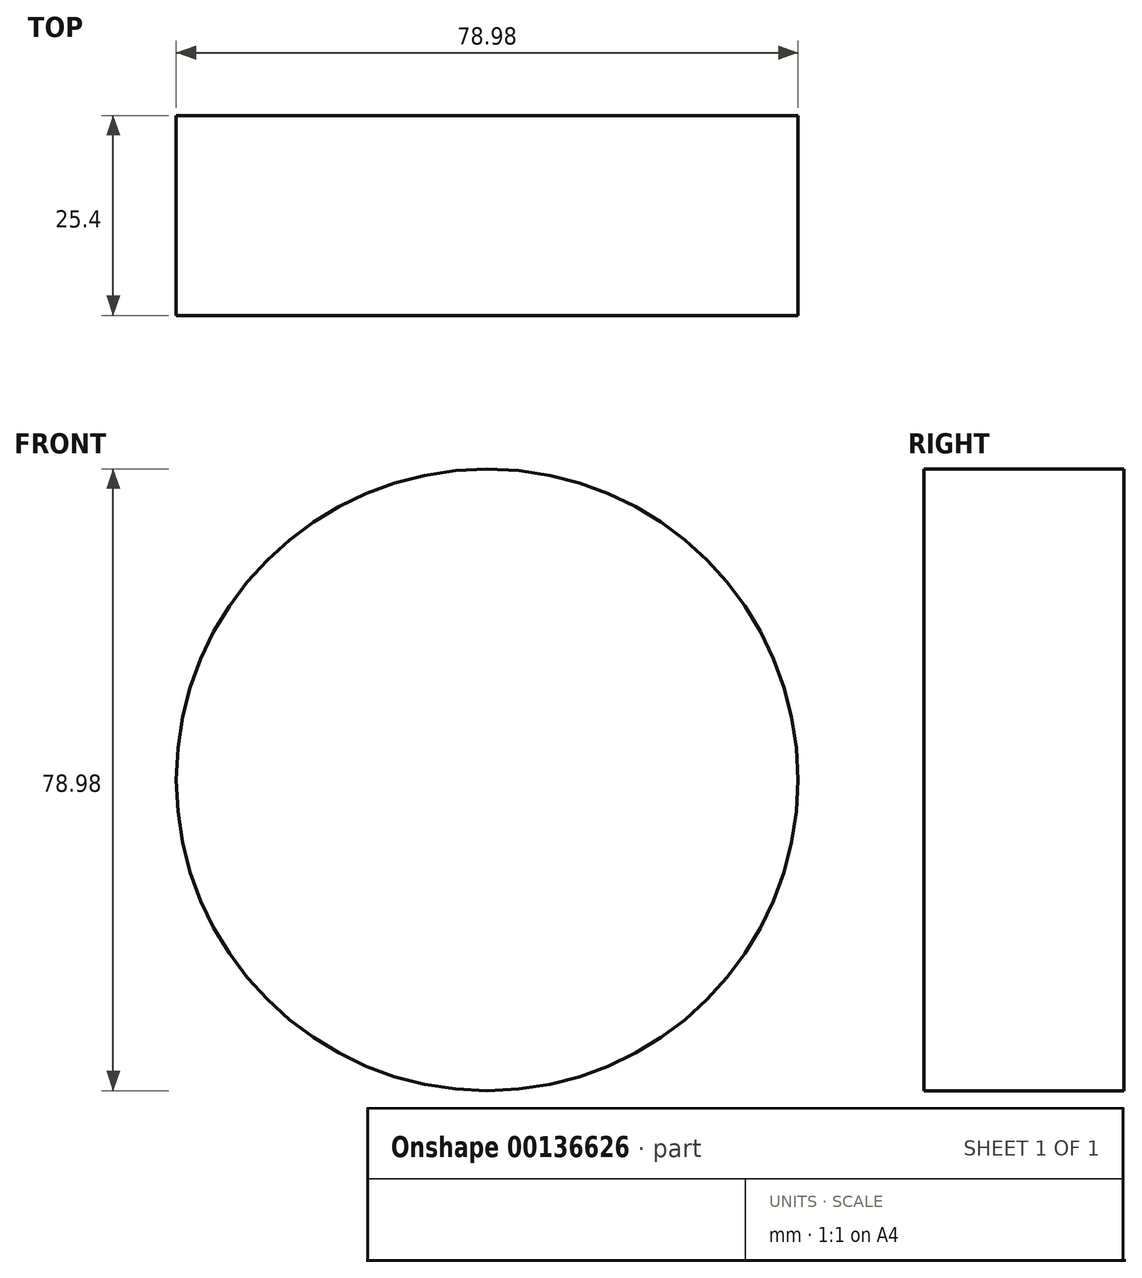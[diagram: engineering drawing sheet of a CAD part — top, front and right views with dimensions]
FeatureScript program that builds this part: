
annotation { "Feature Type Name" : "Feature", "Feature Type Description" : "" }
export const myFeature = defineFeature(function(context is Context, id is Id, definition is map)
    precondition{}
    {
        {
            var Q0;
            Q0=qCreatedBy(makeId("Front.planeOp"),FACE);
            var sketch = newSketch(context, id + "F0", { "sketchPlane" : qUnion([Q0])});
            skCircle(sketch, "E0", {"center": v(0, 0) * mm, "radius": 39.49 * mm});
            skSolve(sketch);
        }
        {
            var Q0;
            Q0 = qSketchRegion(id + "F0", true);
            extrude(context, id + "F1", {"entities" : qUnion([Q0]), "depth" : 25.4 * mm});
        }
    });
